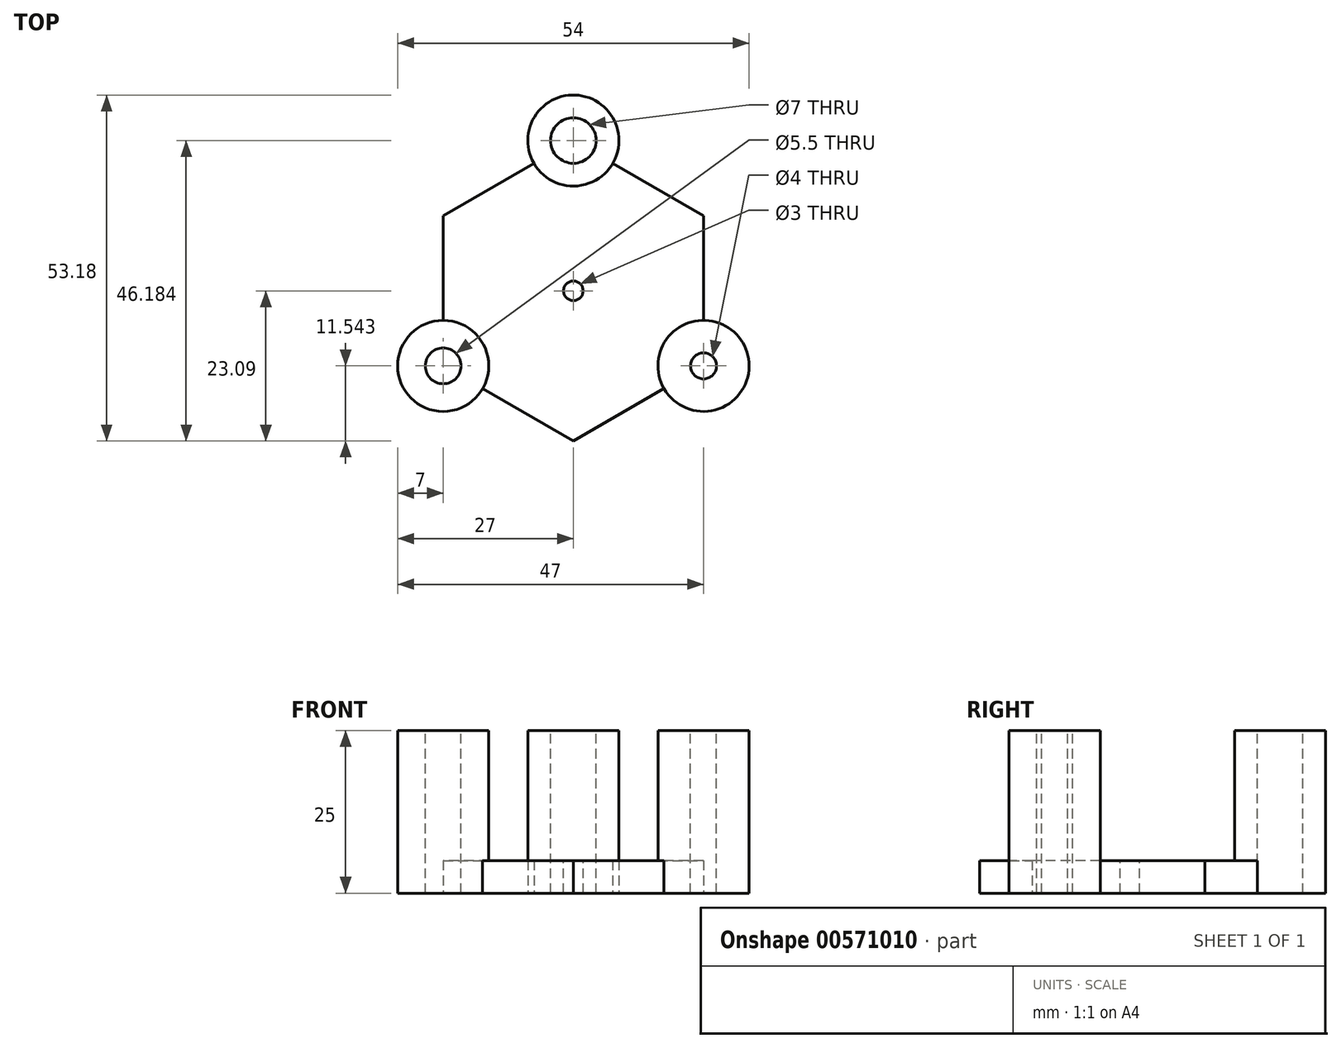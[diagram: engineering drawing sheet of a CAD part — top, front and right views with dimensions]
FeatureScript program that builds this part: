
annotation { "Feature Type Name" : "Feature", "Feature Type Description" : "" }
export const myFeature = defineFeature(function(context is Context, id is Id, definition is map)
    precondition{}
    {
        {
            var Q0;
            Q0=qCreatedBy(makeId("Top.planeOp"),FACE);
            var sketch = newSketch(context, id + "F0", { "sketchPlane" : qUnion([Q0])});
            skCircle(sketch, "E0.cCircle", {"center": v(0, 0) * mm, "radius": 20 * mm, "construction": true});
            skLineSegment(sketch, "E0.0", {"start": v(20, 11.55) * mm, "end": v(20, -11.55) * mm});
            skLineSegment(sketch, "E0.1", {"start": v(20, -11.55) * mm, "end": v(0, -23.1) * mm});
            skLineSegment(sketch, "E0.2", {"start": v(0, -23.1) * mm, "end": v(-20, -11.55) * mm});
            skLineSegment(sketch, "E0.3", {"start": v(-20, -11.55) * mm, "end": v(-20, 11.55) * mm});
            skLineSegment(sketch, "E0.4", {"start": v(-20, 11.55) * mm, "end": v(0, 23.1) * mm});
            skLineSegment(sketch, "E0.5", {"start": v(0, 23.1) * mm, "end": v(20, 11.55) * mm});
            skPoint(sketch, "E0.0.midPoint", {"position": v(20, 0) * mm});
            skCircle(sketch, "E1", {"center": v(0, 23.1) * mm, "radius": 7 * mm});
            skCircle(sketch, "E2", {"center": v(-20, -11.55) * mm, "radius": 7 * mm});
            skCircle(sketch, "E3", {"center": v(20, -11.55) * mm, "radius": 7 * mm});
            skSolve(sketch);
        }
        {
            var Q0;
            {var subQ11=sQuery(id+"F0.wireOp",EDGE,"E0.5");var subQ12=sQuery(id+"F0.wireOp",EDGE,"E0.0");var subQ13=makeQuery(id+"F0.imprint","INTERSECT",VERTEX,{"derivedFrom":[subQ12,subQ11]});Q0=makeQuery(id+"F0.imprint","IMPRINT",FACE,{"disambiguationData":[TD([[makeQuery(id+"F0.imprint","IMPRINT",EDGE,{"disambiguationData":[TD([[subQ13,-1.0]])],"derivedFrom":subQ12}),-1.0]])]});}
            extrude(context, id + "F1", {"entities" : qUnion([Q0]), "depth" : 5 * mm, "offsetDistance" : 25 * mm});
        }
        {
            var Q0;
            {var subQ0=sQuery(id+"F0.wireOp",EDGE,"E0.3");var subQ1=sQuery(id+"F0.wireOp",EDGE,"E0.2");var subQ2=makeQuery(id+"F0.imprint","INTERSECT",VERTEX,{"derivedFrom":[subQ1,subQ0]});Q0=makeQuery(id+"F0.imprint","IMPRINT",FACE,{"disambiguationData":[TD([[makeQuery(id+"F0.imprint","IMPRINT",EDGE,{"disambiguationData":[TD([[subQ2,1.0]])],"derivedFrom":subQ1}),1.0]])]});}
            var Q1;
            {var subQ0=sQuery(id+"F0.wireOp",EDGE,"E0.3");var subQ1=sQuery(id+"F0.wireOp",EDGE,"E0.2");var subQ2=makeQuery(id+"F0.imprint","INTERSECT",VERTEX,{"derivedFrom":[subQ1,subQ0]});Q1=makeQuery(id+"F0.imprint","IMPRINT",FACE,{"disambiguationData":[TD([[makeQuery(id+"F0.imprint","IMPRINT",EDGE,{"disambiguationData":[TD([[subQ2,1.0]])],"derivedFrom":subQ1}),-1.0]])]});}
            var Q2;
            {var subQ0=sQuery(id+"F0.wireOp",EDGE,"E0.5");var subQ1=sQuery(id+"F0.wireOp",EDGE,"E0.4");var subQ2=makeQuery(id+"F0.imprint","INTERSECT",VERTEX,{"derivedFrom":[subQ1,subQ0]});Q2=makeQuery(id+"F0.imprint","IMPRINT",FACE,{"disambiguationData":[TD([[makeQuery(id+"F0.imprint","IMPRINT",EDGE,{"disambiguationData":[TD([[subQ2,1.0]])],"derivedFrom":subQ1}),1.0]])]});}
            var Q3;
            {var subQ0=sQuery(id+"F0.wireOp",EDGE,"E0.5");var subQ1=sQuery(id+"F0.wireOp",EDGE,"E0.4");var subQ2=makeQuery(id+"F0.imprint","INTERSECT",VERTEX,{"derivedFrom":[subQ1,subQ0]});Q3=makeQuery(id+"F0.imprint","IMPRINT",FACE,{"disambiguationData":[TD([[makeQuery(id+"F0.imprint","IMPRINT",EDGE,{"disambiguationData":[TD([[subQ2,1.0]])],"derivedFrom":subQ1}),-1.0]])]});}
            var Q4;
            {var subQ0=sQuery(id+"F0.wireOp",EDGE,"E0.1");var subQ1=sQuery(id+"F0.wireOp",EDGE,"E0.0");var subQ2=makeQuery(id+"F0.imprint","INTERSECT",VERTEX,{"derivedFrom":[subQ1,subQ0]});Q4=makeQuery(id+"F0.imprint","IMPRINT",FACE,{"disambiguationData":[TD([[makeQuery(id+"F0.imprint","IMPRINT",EDGE,{"disambiguationData":[TD([[subQ2,1.0]])],"derivedFrom":subQ1}),1.0]])]});}
            var Q5;
            {var subQ0=sQuery(id+"F0.wireOp",EDGE,"E0.1");var subQ1=sQuery(id+"F0.wireOp",EDGE,"E0.0");var subQ2=makeQuery(id+"F0.imprint","INTERSECT",VERTEX,{"derivedFrom":[subQ1,subQ0]});Q5=makeQuery(id+"F0.imprint","IMPRINT",FACE,{"disambiguationData":[TD([[makeQuery(id+"F0.imprint","IMPRINT",EDGE,{"disambiguationData":[TD([[subQ2,1.0]])],"derivedFrom":subQ1}),-1.0]])]});}
            extrude(context, id + "F2", {"entities" : qUnion([Q0, Q1, Q2, Q3, Q4, Q5]), "operationType" : NewBodyOperationType.ADD, "depth" : 25 * mm, "offsetDistance" : 25 * mm});
        }
        {
            var Q0;
            Q0=sQuery(id+"F0.wireOp",VERTEX,"E0.4.end");
            var Q1;
            Q1=makeQuery(id+"F1.opExtrude","SWEPT_BODY",BODY,{"disambiguationData":[OSD([sQuery(id+"F0.wireOp",EDGE,"E0.0"),sQuery(id+"F0.wireOp",EDGE,"E0.1"),sQuery(id+"F0.wireOp",EDGE,"E0.2"),sQuery(id+"F0.wireOp",EDGE,"E0.3"),sQuery(id+"F0.wireOp",EDGE,"E0.4"),sQuery(id+"F0.wireOp",EDGE,"E0.5"),sQuery(id+"F0.wireOp",EDGE,"E1"),sQuery(id+"F0.wireOp",EDGE,"E2"),sQuery(id+"F0.wireOp",EDGE,"E3")])]});
            hole(context, id + "F3", {"style" : HoleStyle.SIMPLE, "endStyle" : HoleEndStyle.THROUGH, "oppositeDirection" : true, "holeDiameter" : 7 * mm, "majorDiameter" : 5 * mm, "isTappedThrough" : true, "tappedDepth" : 26.25 * mm, "tapClearance" : 3, "locations" : qUnion([Q0]), "scope" : qUnion([Q1]), "startStyle" : HoleStartStyle.PART});
        }
        {
            var Q0;
            Q0=sQuery(id+"F0.wireOp",VERTEX,"E0.2.end");
            var Q1;
            Q1=makeQuery(id+"F1.opExtrude","SWEPT_BODY",BODY,{"disambiguationData":[OSD([sQuery(id+"F0.wireOp",EDGE,"E0.0"),sQuery(id+"F0.wireOp",EDGE,"E0.1"),sQuery(id+"F0.wireOp",EDGE,"E0.2"),sQuery(id+"F0.wireOp",EDGE,"E0.3"),sQuery(id+"F0.wireOp",EDGE,"E0.4"),sQuery(id+"F0.wireOp",EDGE,"E0.5"),sQuery(id+"F0.wireOp",EDGE,"E1"),sQuery(id+"F0.wireOp",EDGE,"E2"),sQuery(id+"F0.wireOp",EDGE,"E3")])]});
            hole(context, id + "F4", {"style" : HoleStyle.SIMPLE, "endStyle" : HoleEndStyle.THROUGH, "oppositeDirection" : true, "holeDiameter" : 5.5 * mm, "majorDiameter" : 5 * mm, "isTappedThrough" : true, "tappedDepth" : 26.25 * mm, "tapClearance" : 3, "locations" : qUnion([Q0]), "scope" : qUnion([Q1]), "startStyle" : HoleStartStyle.PART});
        }
        {
            var Q0;
            Q0=sQuery(id+"F0.wireOp",VERTEX,"E0.0.end");
            var Q1;
            Q1=makeQuery(id+"F1.opExtrude","SWEPT_BODY",BODY,{"disambiguationData":[OSD([sQuery(id+"F0.wireOp",EDGE,"E0.0"),sQuery(id+"F0.wireOp",EDGE,"E0.1"),sQuery(id+"F0.wireOp",EDGE,"E0.2"),sQuery(id+"F0.wireOp",EDGE,"E0.3"),sQuery(id+"F0.wireOp",EDGE,"E0.4"),sQuery(id+"F0.wireOp",EDGE,"E0.5"),sQuery(id+"F0.wireOp",EDGE,"E1"),sQuery(id+"F0.wireOp",EDGE,"E2"),sQuery(id+"F0.wireOp",EDGE,"E3")])]});
            hole(context, id + "F5", {"style" : HoleStyle.SIMPLE, "endStyle" : HoleEndStyle.THROUGH, "oppositeDirection" : true, "holeDiameter" : 4 * mm, "majorDiameter" : 5 * mm, "isTappedThrough" : true, "tappedDepth" : 26.25 * mm, "tapClearance" : 3, "locations" : qUnion([Q0]), "scope" : qUnion([Q1]), "startStyle" : HoleStartStyle.PART});
        }
        {
            var Q0;
            Q0=sQuery(id+"F0.wireOp",VERTEX,"E0.cCircle.center");
            var Q1;
            Q1=makeQuery(id+"F1.opExtrude","SWEPT_BODY",BODY,{"disambiguationData":[OSD([sQuery(id+"F0.wireOp",EDGE,"E0.0"),sQuery(id+"F0.wireOp",EDGE,"E0.1"),sQuery(id+"F0.wireOp",EDGE,"E0.2"),sQuery(id+"F0.wireOp",EDGE,"E0.3"),sQuery(id+"F0.wireOp",EDGE,"E0.4"),sQuery(id+"F0.wireOp",EDGE,"E0.5"),sQuery(id+"F0.wireOp",EDGE,"E1"),sQuery(id+"F0.wireOp",EDGE,"E2"),sQuery(id+"F0.wireOp",EDGE,"E3")])]});
            hole(context, id + "F6", {"style" : HoleStyle.SIMPLE, "endStyle" : HoleEndStyle.THROUGH, "oppositeDirection" : true, "holeDiameter" : 3 * mm, "majorDiameter" : 5 * mm, "isTappedThrough" : true, "tappedDepth" : 26.25 * mm, "tapClearance" : 3, "locations" : qUnion([Q0]), "scope" : qUnion([Q1]), "startStyle" : HoleStartStyle.PART});
        }
    });
